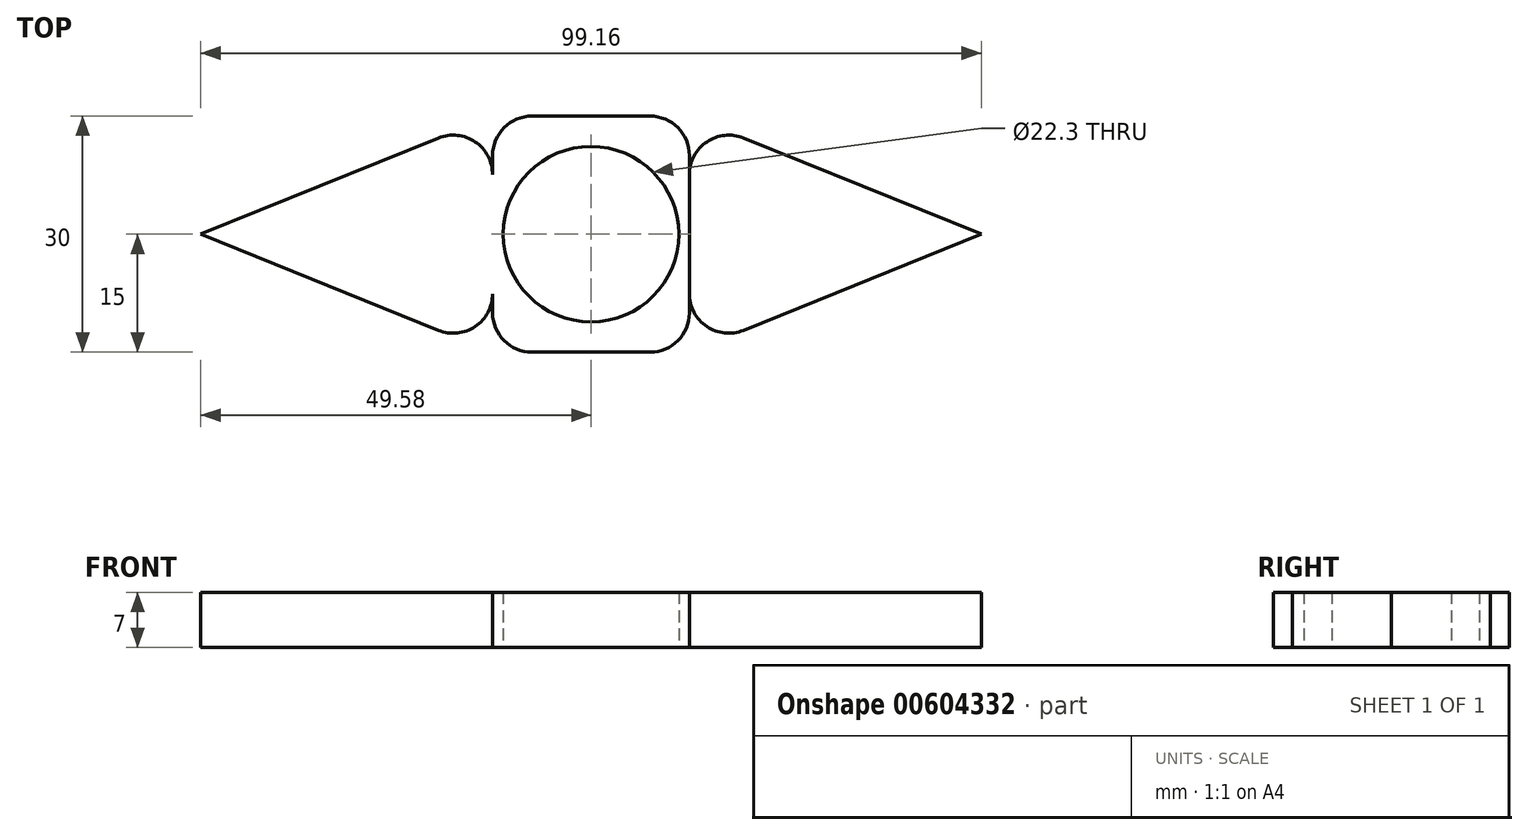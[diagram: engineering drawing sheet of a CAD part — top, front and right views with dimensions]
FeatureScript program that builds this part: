
annotation { "Feature Type Name" : "Feature", "Feature Type Description" : "" }
export const myFeature = defineFeature(function(context is Context, id is Id, definition is map)
    precondition{}
    {
        {
            var Q0;
            Q0=qCreatedBy(makeId("Top.planeOp"),FACE);
            var sketch = newSketch(context, id + "F0", { "sketchPlane" : qUnion([Q0])});
            skLineSegment(sketch, "E0", {"start": v(0, 0) * mm, "end": v(-50, 0) * mm});
            skLineSegment(sketch, "E1", {"start": v(-50, 0) * mm, "end": v(0, 0) * mm});
            skLineSegment(sketch, "E2", {"start": v(50, 0) * mm, "end": v(0, 0) * mm});
            skSolve(sketch);
        }
        {
            var Q0;
            Q0=qCreatedBy(makeId("Top.planeOp"),FACE);
            var sketch = newSketch(context, id + "F1", { "sketchPlane" : qUnion([Q0])});
            skLineSegment(sketch, "E3.bottom", {"start": v(7.5, 15) * mm, "end": v(-7.5, 15) * mm});
            skLineSegment(sketch, "E3.top", {"start": v(7.5, -15) * mm, "end": v(-7.5, -15) * mm});
            skLineSegment(sketch, "E3.left", {"start": v(12.5, 10) * mm, "end": v(12.5, -10) * mm});
            skLineSegment(sketch, "E3.right", {"start": v(-12.5, 10) * mm, "end": v(-12.5, -10) * mm});
            skPoint(sketch, "E3.middle", {"position": v(0, 0) * mm});
            skPoint(sketch, "E4.visualSharp", {"position": v(12.5, 15) * mm});
            skArc(sketch, "E4.filletArc", {"start": v(12.5, 10) * mm, "mid": v(11.04, 13.54) * mm, "end": v(7.5, 15) * mm});
            skPoint(sketch, "E5.visualSharp", {"position": v(-12.5, 15) * mm});
            skArc(sketch, "E5.filletArc", {"start": v(-7.5, 15) * mm, "mid": v(-11.04, 13.54) * mm, "end": v(-12.5, 10) * mm});
            skPoint(sketch, "E6.visualSharp", {"position": v(-12.5, -15) * mm});
            skArc(sketch, "E6.filletArc", {"start": v(-12.5, -10) * mm, "mid": v(-11.04, -13.54) * mm, "end": v(-7.5, -15) * mm});
            skPoint(sketch, "E7.visualSharp", {"position": v(12.5, -15) * mm});
            skArc(sketch, "E7.filletArc", {"start": v(7.5, -15) * mm, "mid": v(11.04, -13.54) * mm, "end": v(12.5, -10) * mm});
            skLineSegment(sketch, "E8", {"start": v(-19.37, 12.22) * mm, "end": v(-49.58, 0) * mm});
            skLineSegment(sketch, "E9", {"start": v(-49.58, 0) * mm, "end": v(-19.38, -12.22) * mm});
            skLineSegment(sketch, "E10", {"start": v(-12.5, 7.58) * mm, "end": v(-12.5, -7.58) * mm});
            skArc(sketch, "E11.filletArc", {"start": v(-12.5, 7.58) * mm, "mid": v(-14.7, 11.73) * mm, "end": v(-19.38, 12.22) * mm});
            skArc(sketch, "E12.filletArc", {"start": v(-19.38, -12.22) * mm, "mid": v(-14.7, -11.73) * mm, "end": v(-12.5, -7.58) * mm});
            skSolve(sketch);
        }
        {
            var Q0;
            Q0=qCreatedBy(makeId("Top.planeOp"),FACE);
            var sketch = newSketch(context, id + "F2", { "sketchPlane" : qUnion([Q0])});
            skLineSegment(sketch, "E13", {"start": v(0, 0) * mm, "end": v(1.5, 0) * mm});
            skLineSegment(sketch, "E14", {"start": v(1.5, 0) * mm, "end": v(12.5, 0) * mm});
            skLineSegment(sketch, "E15", {"start": v(12.5, 0) * mm, "end": v(12.5, 7.58) * mm});
            skLineSegment(sketch, "E16", {"start": v(19.38, 12.22) * mm, "end": v(49.58, 0) * mm});
            skLineSegment(sketch, "E17", {"start": v(49.58, 0) * mm, "end": v(19.38, -12.22) * mm});
            skLineSegment(sketch, "E18", {"start": v(12.5, -7.58) * mm, "end": v(12.5, 0) * mm});
            skPoint(sketch, "E19.visualSharp", {"position": v(12.5, 15) * mm});
            skArc(sketch, "E19.filletArc", {"start": v(19.38, 12.22) * mm, "mid": v(14.7, 11.73) * mm, "end": v(12.5, 7.58) * mm});
            skPoint(sketch, "E20.visualSharp", {"position": v(12.5, -15) * mm});
            skArc(sketch, "E20.filletArc", {"start": v(12.5, -7.58) * mm, "mid": v(14.7, -11.73) * mm, "end": v(19.38, -12.22) * mm});
            skSolve(sketch);
        }
        {
            var Q0;
            Q0=makeQuery(id+"F1.imprint","IMPRINT",FACE,{"disambiguationData":[TD([[makeQuery(id+"F1.imprint","IMPRINT",EDGE,{"derivedFrom":sQuery(id+"F1.wireOp",EDGE,"E3.bottom")}),1.0]])]});
            var Q1;
            Q1=makeQuery(id+"F1.imprint","IMPRINT",FACE,{"disambiguationData":[TD([[makeQuery(id+"F1.imprint","IMPRINT",EDGE,{"derivedFrom":sQuery(id+"F1.wireOp",EDGE,"E8")}),1.0]])]});
            var Q2;
            Q2=makeQuery(id+"F2.imprint","IMPRINT",FACE,{"disambiguationData":[TD([[makeQuery(id+"F2.imprint","IMPRINT",EDGE,{"derivedFrom":sQuery(id+"F2.wireOp",EDGE,"E15")}),-1.0]])]});
            extrude(context, id + "F3", {"entities" : qUnion([Q0, Q1, Q2]), "depth" : 7 * mm, "offsetDistance" : 25 * mm});
        }
        {
            var Q0;
            Q0=sQuery(id+"F0.wireOp",VERTEX,"E0.start");
            var Q1;
            Q1=makeQuery(id+"F3.opExtrude","SWEPT_BODY",BODY,{"disambiguationData":[OSD([sQuery(id+"F1.wireOp",EDGE,"E3.bottom"),sQuery(id+"F1.wireOp",EDGE,"E3.top"),sQuery(id+"F1.wireOp",EDGE,"E3.left"),sQuery(id+"F1.wireOp",EDGE,"E3.right"),sQuery(id+"F1.wireOp",EDGE,"E4.filletArc"),sQuery(id+"F1.wireOp",EDGE,"E5.filletArc"),sQuery(id+"F1.wireOp",EDGE,"E6.filletArc"),sQuery(id+"F1.wireOp",EDGE,"E7.filletArc"),sQuery(id+"F1.wireOp",EDGE,"E8"),sQuery(id+"F1.wireOp",EDGE,"E9"),sQuery(id+"F1.wireOp",EDGE,"E11.filletArc"),sQuery(id+"F1.wireOp",EDGE,"E12.filletArc")])]});
            hole(context, id + "F4", {"style" : HoleStyle.SIMPLE, "endStyle" : HoleEndStyle.THROUGH, "oppositeDirection" : true, "holeDiameter" : 22.3 * mm, "majorDiameter" : 5 * mm, "isTappedThrough" : true, "tappedDepth" : 12 * mm, "tapClearance" : 3, "locations" : qUnion([Q0]), "scope" : qUnion([Q1])});
        }
    });
